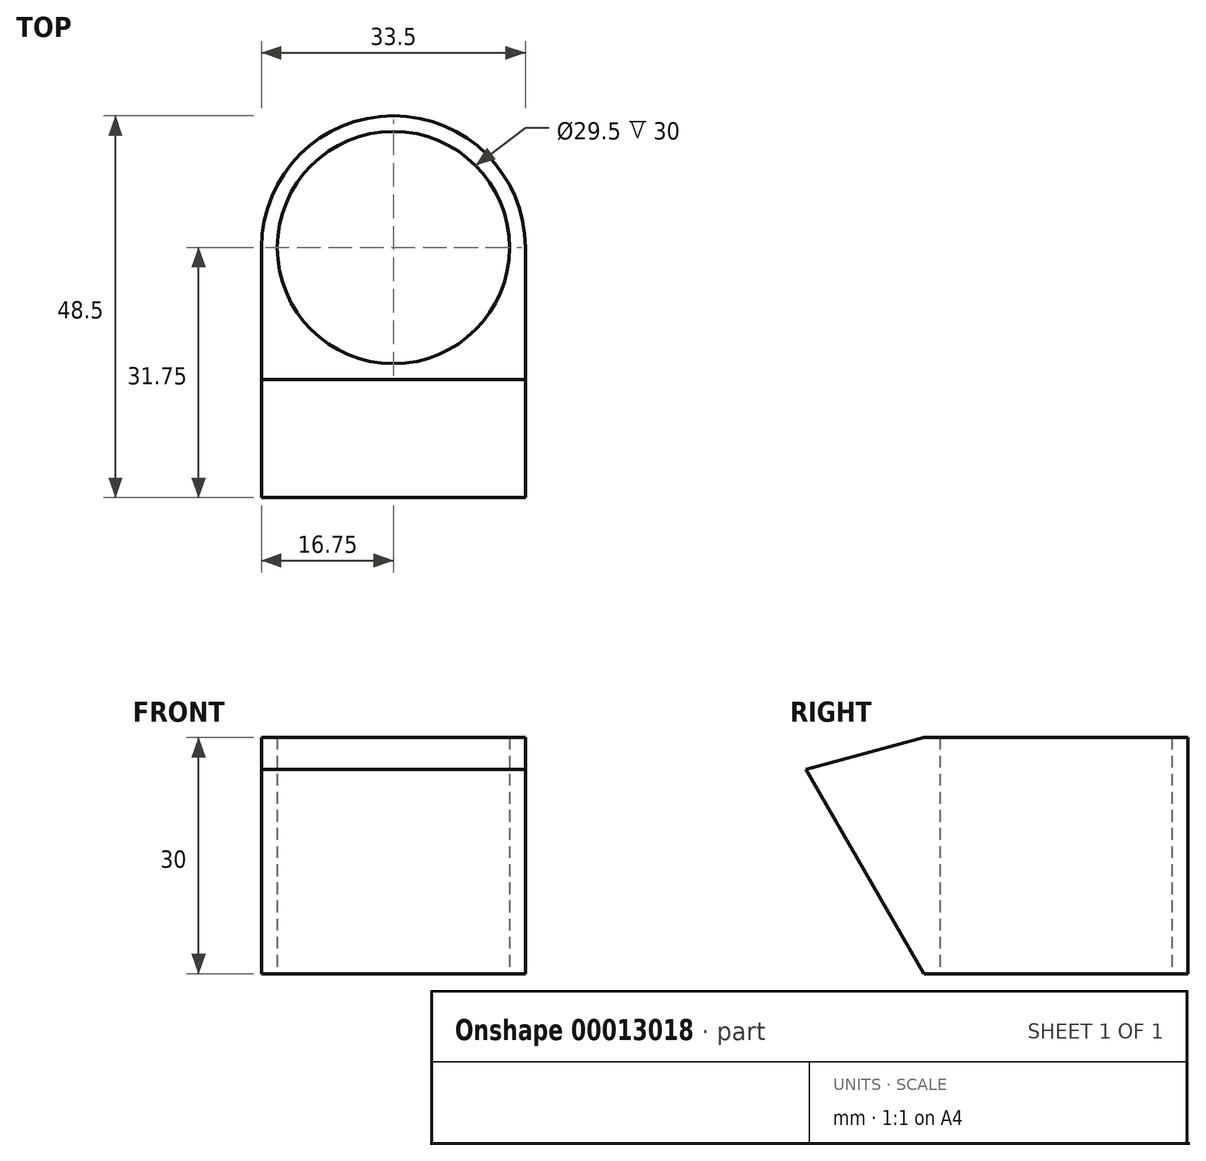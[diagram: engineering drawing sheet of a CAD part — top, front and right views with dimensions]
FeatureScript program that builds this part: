
annotation { "Feature Type Name" : "Feature", "Feature Type Description" : "" }
export const myFeature = defineFeature(function(context is Context, id is Id, definition is map)
    precondition{}
    {
        {
            var Q0;
            Q0=qCreatedBy(makeId("Top.planeOp"),FACE);
            var sketch = newSketch(context, id + "F0", { "sketchPlane" : qUnion([Q0])});
            skCircle(sketch, "E0", {"center": v(0, 0) * mm, "radius": 14.75 * mm});
            skCircle(sketch, "E1", {"center": v(0, 0) * mm, "radius": 16.75 * mm});
            skSolve(sketch);
        }
        {
            var Q0;
            Q0=makeQuery(id+"F0.imprint","IMPRINT",FACE,{"disambiguationData":[TD([[makeQuery(id+"F0.imprint","IMPRINT",EDGE,{"derivedFrom":sQuery(id+"F0.wireOp",EDGE,"E0")}),-1.0]])]});
            extrude(context, id + "F1", {"entities" : qUnion([Q0]), "depth" : 30 * mm});
        }
        {
            var Q0;
            Q0=qCreatedBy(makeId("Right.planeOp"),FACE);
            var sketch = newSketch(context, id + "F2", { "sketchPlane" : qUnion([Q0])});
            skLineSegment(sketch, "E2", {"start": v(0, 0) * mm, "end": v(0, 30) * mm});
            skLineSegment(sketch, "E3", {"start": v(0, 30) * mm, "end": v(-16.75, 30) * mm});
            skLineSegment(sketch, "E4", {"start": v(-16.75, 30) * mm, "end": v(-16.75, 0) * mm});
            skLineSegment(sketch, "E5", {"start": v(-16.75, 0) * mm, "end": v(0, 0) * mm});
            skLineSegment(sketch, "E6", {"start": v(-16.75, 0) * mm, "end": v(-31.75, 25.98) * mm});
            skLineSegment(sketch, "E7", {"start": v(-31.75, 25.98) * mm, "end": v(-16.75, 30) * mm});
            skSolve(sketch);
        }
        {
            var Q0;
            Q0=makeQuery(id+"F2.imprint","IMPRINT",FACE,{"disambiguationData":[TD([[makeQuery(id+"F2.imprint","IMPRINT",EDGE,{"derivedFrom":sQuery(id+"F2.wireOp",EDGE,"E2")}),1.0]])]});
            var Q1;
            Q1=makeQuery(id+"F2.imprint","IMPRINT",FACE,{"disambiguationData":[TD([[makeQuery(id+"F2.imprint","IMPRINT",EDGE,{"derivedFrom":sQuery(id+"F2.wireOp",EDGE,"E4")}),-1.0]])]});
            var Q2;
            Q2=makeQuery(id+"F1.opExtrude","SWEPT_FACE",FACE,{"disambiguationData":[OSD([sQuery(id+"F0.wireOp",EDGE,"E1")])]});
            extrude(context, id + "F3", {"entities" : qUnion([Q0, Q1]), "operationType" : NewBodyOperationType.ADD, "endBound" : BoundingType.SYMMETRIC, "endBoundEntity" : qUnion([Q2]), "depth" : 33.5 * mm});
        }
        {
            var Q0;
            Q0=makeQuery(id+"F0.imprint","IMPRINT",FACE,{"disambiguationData":[TD([[makeQuery(id+"F0.imprint","IMPRINT",EDGE,{"derivedFrom":sQuery(id+"F0.wireOp",EDGE,"E0")}),1.0]])]});
            extrude(context, id + "F4", {"entities" : qUnion([Q0]), "operationType" : NewBodyOperationType.REMOVE, "endBound" : BoundingType.THROUGH_ALL, "depth" : 25 * mm});
        }
    });
